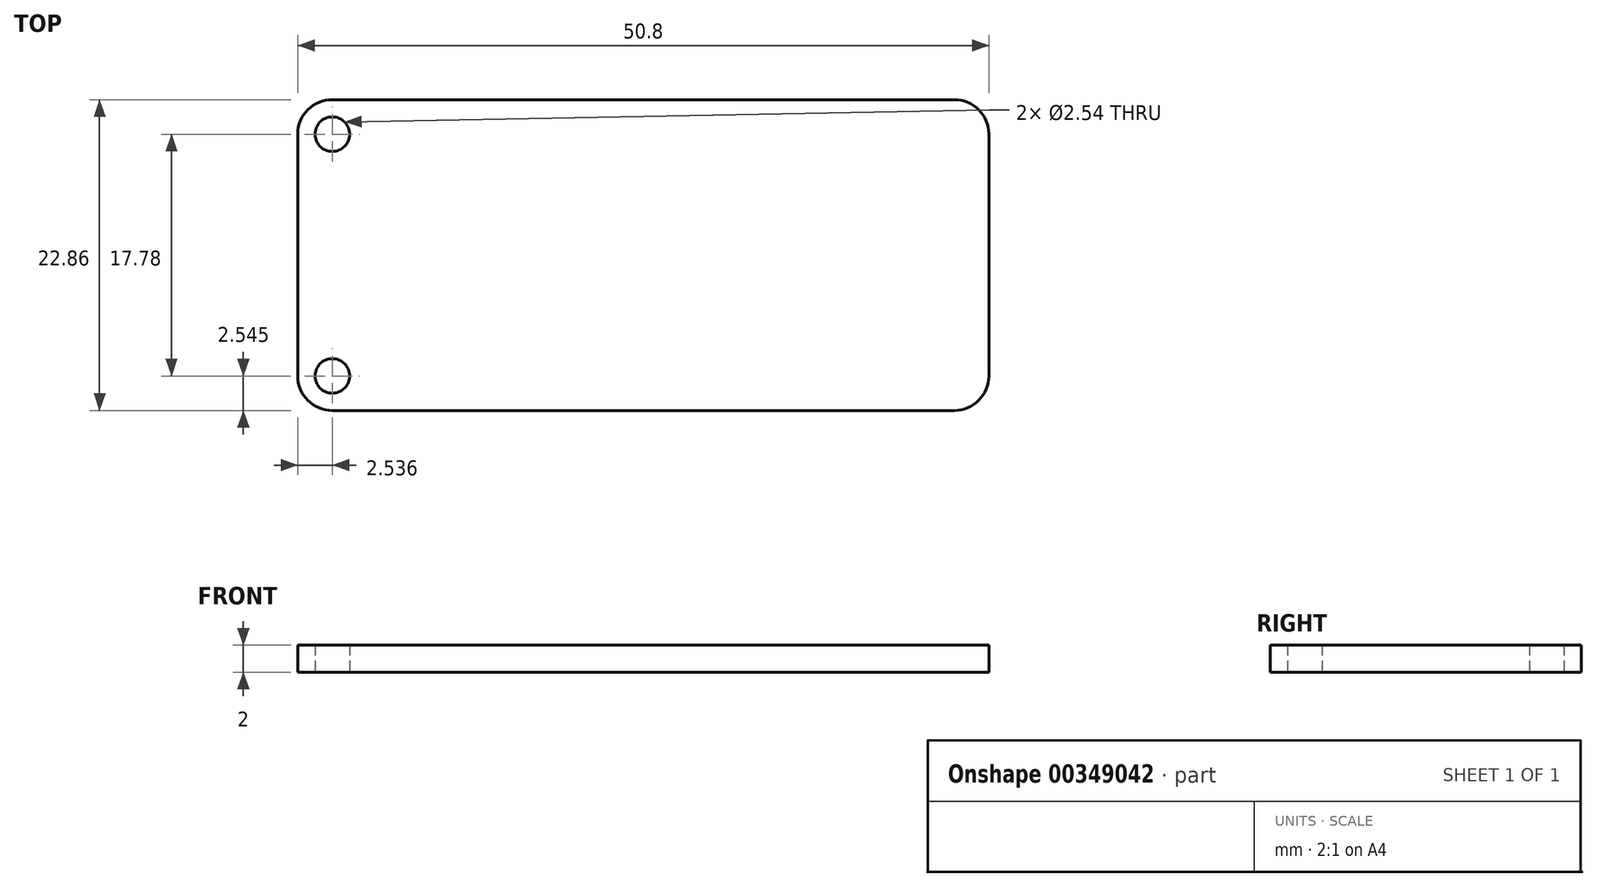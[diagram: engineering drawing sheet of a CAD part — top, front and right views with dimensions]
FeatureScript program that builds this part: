
annotation { "Feature Type Name" : "Feature", "Feature Type Description" : "" }
export const myFeature = defineFeature(function(context is Context, id is Id, definition is map)
    precondition{}
    {
        {
            var Q0;
            Q0=qCreatedBy(makeId("Top.planeOp"),FACE);
            var sketch = newSketch(context, id + "F0", { "sketchPlane" : qUnion([Q0])});
            skLineSegment(sketch, "E0.bottom", {"start": v(10, -12.6) * mm, "end": v(55.72, -12.6) * mm});
            skLineSegment(sketch, "E0.top", {"start": v(10, -35.47) * mm, "end": v(55.72, -35.47) * mm});
            skLineSegment(sketch, "E0.left", {"start": v(7.46, -15.15) * mm, "end": v(7.46, -32.93) * mm});
            skLineSegment(sketch, "E0.right", {"start": v(58.26, -15.15) * mm, "end": v(58.26, -32.93) * mm});
            skPoint(sketch, "E1.visualSharp", {"position": v(7.46, -12.6) * mm});
            skArc(sketch, "E1.filletArc", {"start": v(10, -12.6) * mm, "mid": v(8.2, -13.35) * mm, "end": v(7.46, -15.15) * mm});
            skPoint(sketch, "E2.visualSharp", {"position": v(58.26, -12.6) * mm});
            skArc(sketch, "E2.filletArc", {"start": v(58.26, -15.15) * mm, "mid": v(57.51, -13.35) * mm, "end": v(55.72, -12.6) * mm});
            skPoint(sketch, "E3.visualSharp", {"position": v(58.26, -35.47) * mm});
            skArc(sketch, "E3.filletArc", {"start": v(55.72, -35.47) * mm, "mid": v(57.51, -34.72) * mm, "end": v(58.26, -32.93) * mm});
            skPoint(sketch, "E4.visualSharp", {"position": v(7.46, -35.47) * mm});
            skArc(sketch, "E4.filletArc", {"start": v(7.46, -32.93) * mm, "mid": v(8.2, -34.72) * mm, "end": v(10, -35.47) * mm});
            skCircle(sketch, "E5", {"center": v(10, -15.15) * mm, "radius": 1.27 * mm});
            skCircle(sketch, "E6", {"center": v(10, -32.93) * mm, "radius": 1.27 * mm});
            skPoint(sketch, "E7", {"position": v(7.46, -24.04) * mm});
            skLineSegment(sketch, "E8", {"start": v(7.46, -24.04) * mm, "end": v(58.26, -24.04) * mm});
            skSolve(sketch);
        }
        {
            var Q0;
            Q0=makeQuery(id+"F0.imprint","IMPRINT",FACE,{"disambiguationData":[TD([[makeQuery(id+"F0.imprint","IMPRINT",EDGE,{"derivedFrom":sQuery(id+"F0.wireOp",EDGE,"E0.bottom")}),-1.0]])]});
            var Q1;
            Q1=makeQuery(id+"F0.imprint","IMPRINT",FACE,{"disambiguationData":[TD([[makeQuery(id+"F0.imprint","IMPRINT",EDGE,{"derivedFrom":sQuery(id+"F0.wireOp",EDGE,"E0.top")}),1.0]])]});
            extrude(context, id + "F1", {"entities" : qUnion([Q0, Q1]), "depth" : 2 * mm});
        }
    });
